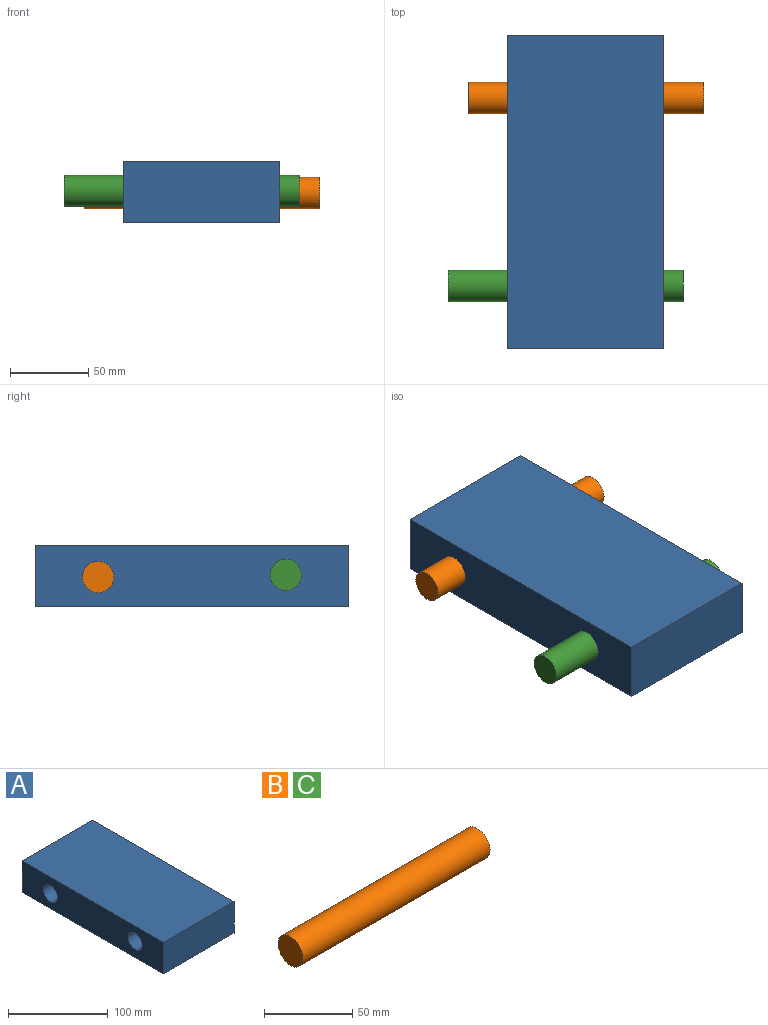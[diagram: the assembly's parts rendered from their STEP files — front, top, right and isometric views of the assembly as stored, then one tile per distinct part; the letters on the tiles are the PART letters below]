
ASSEMBLY  parts=3 mates=2
PART A: 8 faces, bbox 100x200x38.6 mm
  f0: plane 200x38.59mm, normal (-1,0,0), area 7090.3mm2, adj f1,f3,f4,f5,f6,f7
  f1: plane 100x38.59mm, normal (0,-1,0), area 3859.3mm2, adj f0,f2,f4,f5
  f2: plane 200x38.59mm, normal (1,0,0), area 7090.3mm2, adj f1,f3,f4,f5,f6,f7
  f3: plane 100x38.59mm, normal (0,1,0), area 3859.3mm2, adj f0,f2,f4,f5
  f4: plane 200x100mm, normal (0,0,-1), area 20000mm2, adj f0,f1,f2,f3
  f5: plane 200x100mm, normal (0,0,1), area 20000mm2, adj f0,f1,f2,f3
  f6: cylinder r=10mm len=100mm, axis (1,0,0), area 6283.2mm2, adj f0,f2
  f7: cylinder r=10mm len=100mm, axis (1,0,0), area 6283.2mm2, adj f0,f2
PART B: 3 faces, bbox 150x20x20 mm
  f0: cylinder r=10mm len=150mm, axis (1,0,0), area 9424.8mm2, adj f1,f2
  f1: plane 20x20mm, normal (-1,0,0), area 314.2mm2, adj f0
  f2: plane 20x20mm, normal (1,0,0), area 314.2mm2, adj f0
PART C: same geometry as B
PLACE A t=(-11.38,-47.51,49.7)mm
PLACE B t=(113.96,112.49,29.7)mm
PLACE C t=(100.83,-7.51,31.11)mm
MATE cylindrical A.f7 <-> C.f0  axis (1,0,0) through (-11.38,-7.51,31.11)mm
MATE cylindrical B.f0 <-> A.f6  axis (1,0,0) through (38.96,112.49,29.7)mm
